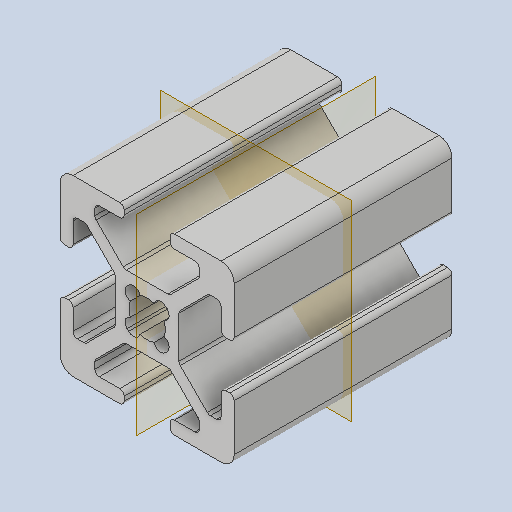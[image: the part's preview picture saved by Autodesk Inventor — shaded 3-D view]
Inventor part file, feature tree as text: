
AUTODESK INVENTOR PART (.ipt)
format: ipt  version: 2023 (Build 270158000, 158)  size: 365,568 bytes
history: native  units: mm
features: plane x2, extrude x1, sketch x1
ambient origin geometry x8: Origin, YZ Plane, XZ Plane, XY Plane, X Axis, Y Axis, Z Axis, Center Point
bodies: Solid1 (feature_tree)
feature tree (4):
  extrude  "Extrusion1"  [1 undecoded]
  plane  "Work Plane1"
  plane  "Work Plane2"
  sketch  "Sketch_1"  dims[d0=25.0mm d1=0.0mm]
note: 1 required parameter value undecoded (feature->parameter linkage not recoverable at this tier; creation-order binding heuristic only, values carry confidence <= 0.55)
